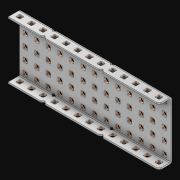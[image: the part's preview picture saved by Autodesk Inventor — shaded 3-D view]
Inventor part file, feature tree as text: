
AUTODESK INVENTOR PART (.ipt)
format: ipt  version: 2021 (Build 250183000, 183)  size: 3,157,504 bytes
history: native  units: in
note: dims shown in document units (in); Inventor stores cm internally (conversion verified against a paired STEP export)
features: extrude x92, other x91, sketch x4, thicken_offset x3, pattern_linear x3, imported_body x1
ambient origin geometry x8: Origin, YZ Plane, XZ Plane, XY Plane, X Axis, Y Axis, Z Axis, Center Point
bodies: Solid1 (feature_tree)
feature tree (194):
  thicken_offset  "Thicken1"
  thicken_offset  "Thicken2"
  thicken_offset  "Thicken3"
  pattern_linear  "Rectangular Pattern1"  Spacing1=0.001in  [1 undecoded]
  pattern_linear  "Rectangular Pattern2"  Spacing1=0.001in  [1 undecoded]
  pattern_linear  "Rectangular Pattern3"  Spacing1=0.182in  [1 undecoded]
  extrude  "Extrusion1"  Depth=0.063in TaperAngle=0.0deg
  sketch  "Sketch1"  dims[d0=0.001in]
  other  "Srf1"
  sketch  "Sketch2"  dims[d1=0.001in]
  other  "Srf2"
  sketch  "Sketch3"  dims[d2=0.001in]
  other  "Srf3"
  other  "Srf4"
  other  "Srf5"
  other  "Srf6"
  other  "Srf7"
  other  "Srf8"
  other  "Srf9"
  other  "Srf10"
  other  "Srf11"
  other  "Srf12"
  other  "Srf13"
  other  "Srf14"
  other  "Srf15"
  other  "Srf38"
  other  "Srf39"
  other  "Srf40"
  other  "Srf41"
  other  "Srf42"
  other  "Srf43"
  other  "Srf44"
  other  "Srf45"
  other  "Srf46"
  other  "Srf47"
  other  "Srf48"
  other  "Srf49"
  other  "Srf72"
  other  "Srf73"
  other  "Srf74"
  other  "Srf75"
  other  "Srf76"
  other  "Srf77"
  other  "Srf78"
  other  "Srf79"
  other  "Srf80"
  other  "Srf81"
  other  "Srf82"
  other  "Srf83"
  other  "Srf106"
  other  "Srf107"
  other  "Srf108"
  other  "Srf109"
  other  "Srf110"
  other  "Srf111"
  other  "Srf112"
  other  "Srf113"
  other  "Srf114"
  other  "Srf115"
  other  "Srf116"
  other  "Srf117"
  other  "Srf118"
  other  "Srf141"
  other  "Srf142"
  other  "Srf143"
  other  "Srf144"
  other  "Srf145"
  other  "Srf146"
  other  "Srf147"
  other  "Srf148"
  other  "Srf149"
  other  "Srf150"
  other  "Srf151"
  other  "Srf152"
  other  "Srf153"
  other  "Srf176"
  other  "Srf177"
  other  "Srf178"
  other  "Srf179"
  other  "Srf180"
  other  "Srf181"
  other  "Srf182"
  other  "Srf183"
  other  "Srf184"
  other  "Srf185"
  other  "Srf186"
  other  "Srf187"
  other  "Srf188"
  other  "Srf211"
  other  "Srf212"
  other  "Srf213"
  other  "Srf214"
  other  "Srf215"
  other  "Srf216"
  other  "Srf217"
  other  "Srf218"
  other  "Srf219"
  other  "Srf220"
  other  "Srf221"
  other  "Srf222"
  other  "Srf223"
  sketch  "Sketch4"  dims[d3=0.001in d4=0.001in d5=0.001in d6=0.182in d7=0.063in d8=0.0in d9=0.182in d10=0.063in d11=0.0in d12=0.182in d13=0.063in d14=0.0in d17=0.5in d18=5.1181in d20=0.5in d21=5.1181in d23=0.5in d24=1.9685in d26=0.5in d27=11.0in d28=0.0in]
  imported_body  "Imported1"
  extrude  "ExtrusionSrf1"  Depth=0.063in
  extrude  "ExtrusionSrf2"  Depth=0.063in TaperAngle=0.0deg
  extrude  "ExtrusionSrf3"  Depth=0.063in
  extrude  "ExtrusionSrf4"  Depth=0.063in TaperAngle=0.0deg
  extrude  "ExtrusionSrf5"  Depth=0.063in
  extrude  "ExtrusionSrf6"  Depth=0.063in
  extrude  "ExtrusionSrf7"  Depth=0.063in
  extrude  "ExtrusionSrf8"  Depth=0.063in
  extrude  "ExtrusionSrf9"  Depth=0.063in
  extrude  "ExtrusionSrf10"  Depth=0.063in
  extrude  "ExtrusionSrf11"  Depth=0.063in
  extrude  "ExtrusionSrf12"  TaperAngle=0.0deg  [1 undecoded]
  extrude  "ExtrusionSrf13"  [1 undecoded]
  extrude  "ExtrusionSrf14"  [1 undecoded]
  extrude  "ExtrusionSrf15"  [1 undecoded]
  extrude  "ExtrusionSrf38"  [1 undecoded]
  extrude  "ExtrusionSrf39"  [1 undecoded]
  extrude  "ExtrusionSrf40"  [1 undecoded]
  extrude  "ExtrusionSrf41"  [1 undecoded]
  extrude  "ExtrusionSrf42"  [1 undecoded]
  extrude  "ExtrusionSrf43"  [1 undecoded]
  extrude  "ExtrusionSrf44"  [1 undecoded]
  extrude  "ExtrusionSrf45"  [1 undecoded]
  extrude  "ExtrusionSrf46"  [1 undecoded]
  extrude  "ExtrusionSrf47"  [1 undecoded]
  extrude  "ExtrusionSrf48"  [1 undecoded]
  extrude  "ExtrusionSrf49"  [1 undecoded]
  extrude  "ExtrusionSrf72"  [1 undecoded]
  extrude  "ExtrusionSrf73"  [1 undecoded]
  extrude  "ExtrusionSrf74"  [1 undecoded]
  extrude  "ExtrusionSrf75"  [1 undecoded]
  extrude  "ExtrusionSrf76"  [1 undecoded]
  extrude  "ExtrusionSrf77"  [1 undecoded]
  extrude  "ExtrusionSrf78"  [1 undecoded]
  extrude  "ExtrusionSrf79"  [1 undecoded]
  extrude  "ExtrusionSrf80"  [1 undecoded]
  extrude  "ExtrusionSrf81"  [1 undecoded]
  extrude  "ExtrusionSrf82"  [1 undecoded]
  extrude  "ExtrusionSrf83"  [1 undecoded]
  extrude  "ExtrusionSrf106"  [1 undecoded]
  extrude  "ExtrusionSrf107"  [1 undecoded]
  extrude  "ExtrusionSrf108"  [1 undecoded]
  extrude  "ExtrusionSrf109"  [1 undecoded]
  extrude  "ExtrusionSrf110"  [1 undecoded]
  extrude  "ExtrusionSrf111"  [1 undecoded]
  extrude  "ExtrusionSrf112"  [1 undecoded]
  extrude  "ExtrusionSrf113"  [1 undecoded]
  extrude  "ExtrusionSrf114"  [1 undecoded]
  extrude  "ExtrusionSrf115"  [1 undecoded]
  extrude  "ExtrusionSrf116"  [1 undecoded]
  extrude  "ExtrusionSrf117"  [1 undecoded]
  extrude  "ExtrusionSrf118"  [1 undecoded]
  extrude  "ExtrusionSrf141"  [1 undecoded]
  extrude  "ExtrusionSrf142"  [1 undecoded]
  extrude  "ExtrusionSrf143"  [1 undecoded]
  extrude  "ExtrusionSrf144"  [1 undecoded]
  extrude  "ExtrusionSrf145"  [1 undecoded]
  extrude  "ExtrusionSrf146"  [1 undecoded]
  extrude  "ExtrusionSrf147"  [1 undecoded]
  extrude  "ExtrusionSrf148"  [1 undecoded]
  extrude  "ExtrusionSrf149"  [1 undecoded]
  extrude  "ExtrusionSrf150"  [1 undecoded]
  extrude  "ExtrusionSrf151"  [1 undecoded]
  extrude  "ExtrusionSrf152"  [1 undecoded]
  extrude  "ExtrusionSrf153"  [1 undecoded]
  extrude  "ExtrusionSrf176"  [1 undecoded]
  extrude  "ExtrusionSrf177"  [1 undecoded]
  extrude  "ExtrusionSrf178"  [1 undecoded]
  extrude  "ExtrusionSrf179"  [1 undecoded]
  extrude  "ExtrusionSrf180"  [1 undecoded]
  extrude  "ExtrusionSrf181"  [1 undecoded]
  extrude  "ExtrusionSrf182"  [1 undecoded]
  extrude  "ExtrusionSrf183"  [1 undecoded]
  extrude  "ExtrusionSrf184"  [1 undecoded]
  extrude  "ExtrusionSrf185"  [1 undecoded]
  extrude  "ExtrusionSrf186"  [1 undecoded]
  extrude  "ExtrusionSrf187"  [1 undecoded]
  extrude  "ExtrusionSrf188"  [1 undecoded]
  extrude  "ExtrusionSrf211"  [1 undecoded]
  extrude  "ExtrusionSrf212"  [1 undecoded]
  extrude  "ExtrusionSrf213"  [1 undecoded]
  extrude  "ExtrusionSrf214"  [1 undecoded]
  extrude  "ExtrusionSrf215"  [1 undecoded]
  extrude  "ExtrusionSrf216"  [1 undecoded]
  extrude  "ExtrusionSrf217"  [1 undecoded]
  extrude  "ExtrusionSrf218"  [1 undecoded]
  extrude  "ExtrusionSrf219"  [1 undecoded]
  extrude  "ExtrusionSrf220"  [1 undecoded]
  extrude  "ExtrusionSrf221"  [1 undecoded]
  extrude  "ExtrusionSrf222"  [1 undecoded]
  extrude  "ExtrusionSrf223"  [1 undecoded]
note: 83 required parameter values undecoded (feature->parameter linkage not recoverable at this tier; creation-order binding heuristic only, values carry confidence <= 0.55)
